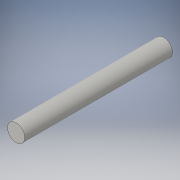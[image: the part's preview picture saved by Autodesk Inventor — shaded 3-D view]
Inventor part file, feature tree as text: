
AUTODESK INVENTOR PART (.ipt)
format: ipt  version: 2016 (Build 200138000, 138)  size: 86,528 bytes
history: native  units: in
note: dims shown in document units (in); Inventor stores cm internally (conversion verified against a paired STEP export)
features: extrude x1, sketch x1
ambient origin geometry x8: Origin, YZ Plane, XZ Plane, XY Plane, X Axis, Y Axis, Z Axis, Center Point
bodies: Solid1 (feature_tree)
feature tree (2):
  extrude  "Extrusion1"  Depth=1.5in TaperAngle=0.0deg
  sketch  "Sketch1"  dims[d0=0.175in d1=1.5in d2=0.0in]
